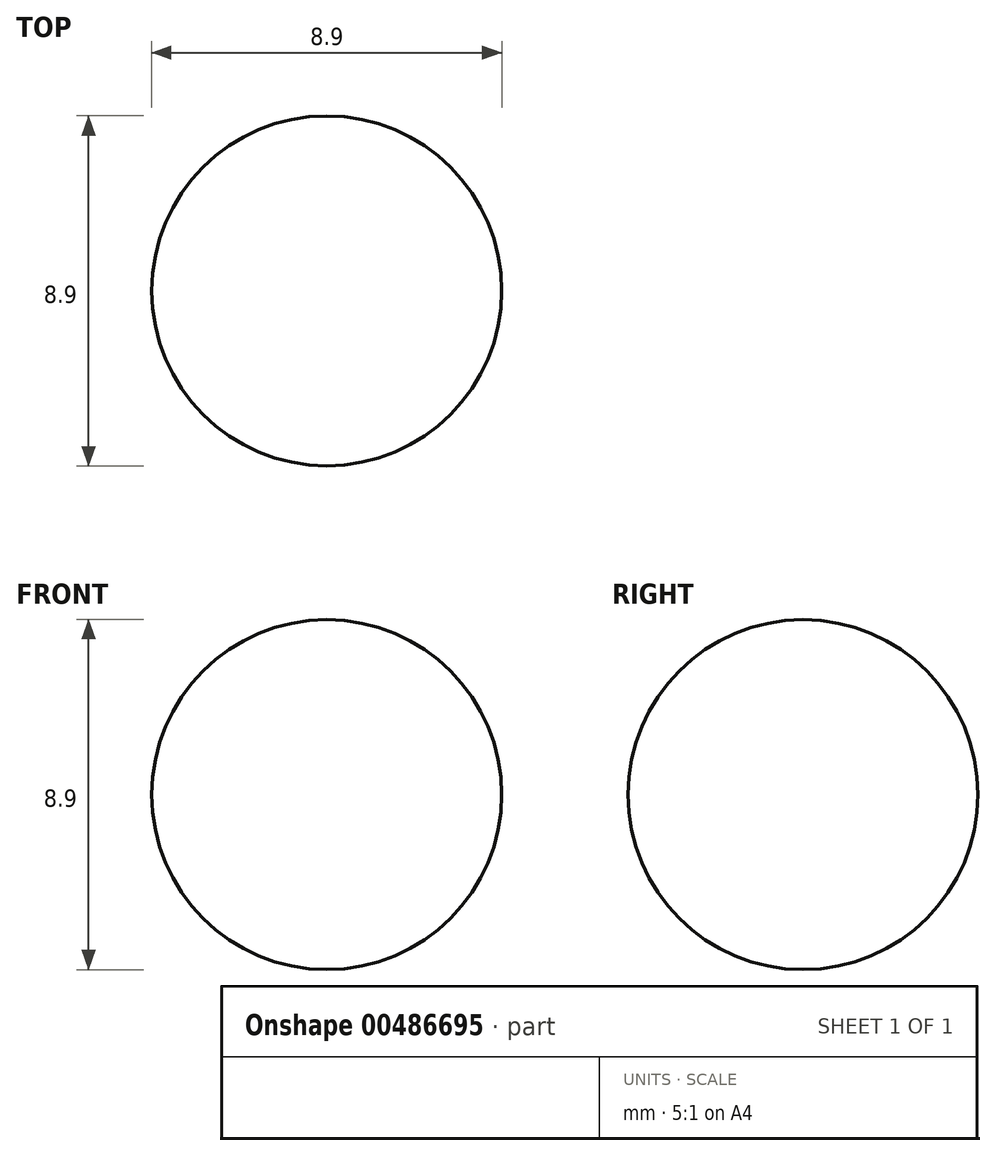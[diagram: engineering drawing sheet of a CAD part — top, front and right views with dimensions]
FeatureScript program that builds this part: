
annotation { "Feature Type Name" : "Feature", "Feature Type Description" : "" }
export const myFeature = defineFeature(function(context is Context, id is Id, definition is map)
    precondition{}
    {
        {
            var Q0;
            Q0=qCreatedBy(makeId("Top.planeOp"),FACE);
            var sketch = newSketch(context, id + "F0", { "sketchPlane" : qUnion([Q0])});
            skArc(sketch, "E0", {"start": v(0, 4.45) * mm, "mid": v(-4.45, 0) * mm, "end": v(0, -4.45) * mm});
            skLineSegment(sketch, "E1", {"start": v(0, 4.45) * mm, "end": v(0, -4.45) * mm});
            skSolve(sketch);
        }
        {
            var Q0;
            Q0=makeQuery(id+"F0.imprint","IMPRINT",FACE,{"disambiguationData":[TD([[makeQuery(id+"F0.imprint","IMPRINT",EDGE,{"derivedFrom":sQuery(id+"F0.wireOp",EDGE,"E0")}),1.0]])]});
            var Q1;
            Q1=sQuery(id+"F0.wireOp",EDGE,"E1");
            revolve(context, id + "F1", {"entities" : qUnion([Q0]), "axis" : qUnion([Q1]), "revolveType" : RevolveType.FULL});
        }
    });
